# Revit family: WASHTECH 2019 CDe120L
name_source: partatom
category: Specialty Equipment
revit_build: Autodesk Revit 2017 (Build: 20160225_1515(x64)
units: mm (PartAtom-declared; Revit-internal decimal feet)

## family parameters
Always vertical = Yes
Cut with Voids When Loaded = No
Part Type = Normal
Room Calculation Point = No
Round Connector Dimension = Use Diameter
Shared = No
Work Plane-Based = No

## types (1)
- WASHTECH 2019 CDe120L
    Apparent Power = 24220 VA
    Cold Water Sizes = 1"
    Conn Conduit = Yes
    Cycle = 50 Hz
    Description = RACK CONVEYOR DISHWASHER
    FL Amps = 35 A
    Hot Water Connection Height = 0 mm  [stored 0 ft]
    Hot Water Size = 1"
    Indirect Waste Connection Height = 0 mm  [stored 0 ft]
    Indirect Waste Size = 2"
    Manufacturer = WASHTECH\STARLINE
    Max Overcurrent Protection = 0 A
    Min Ckt Ampacity = 0 A
    Model = CDe120L
    Phase = 3
    Volts = 400 V
    Watts = 24220 W
    Weight in kgs = 245

note: [stored X ft] marks values corroborated as IEEE doubles in the binary element streams (Revit-internal decimal feet)

## geometry (parser evidence)
native form markers: Blend x10, Sweep x2
no freeform markers — native parametric forms only
